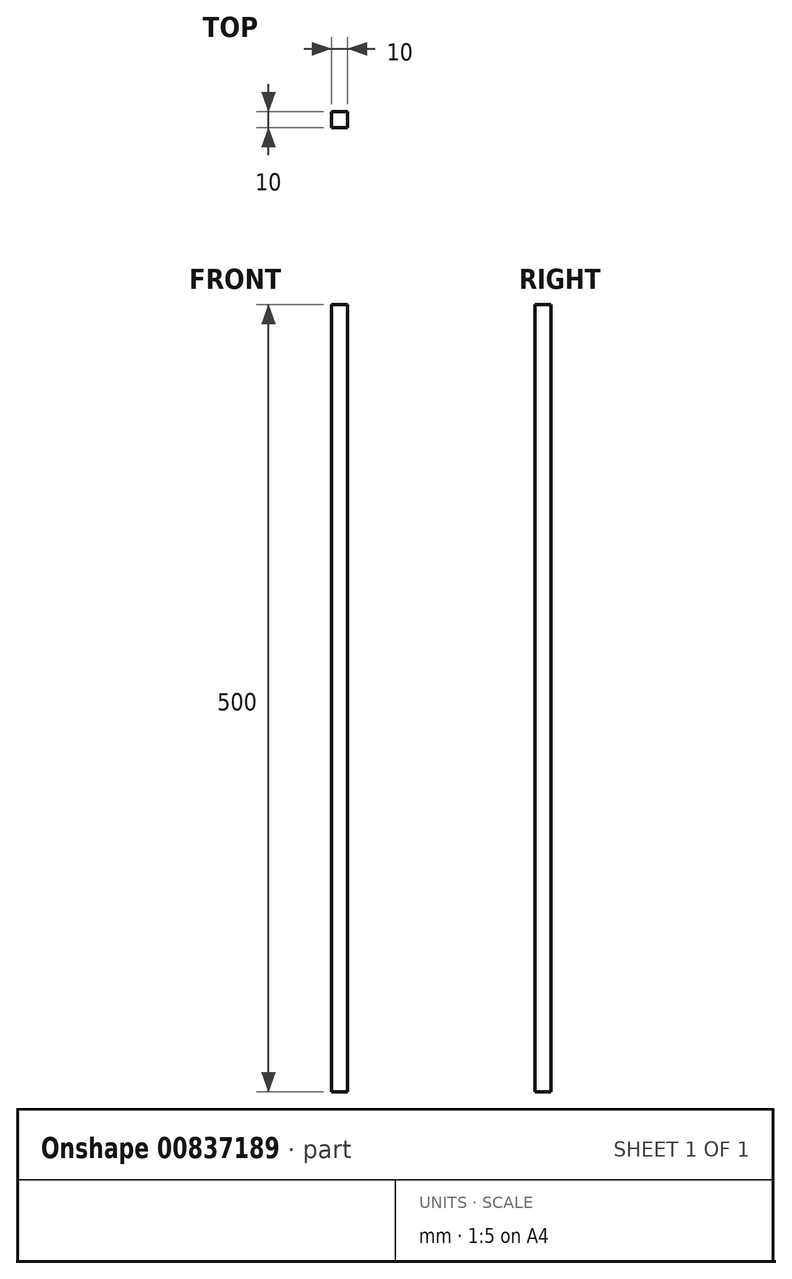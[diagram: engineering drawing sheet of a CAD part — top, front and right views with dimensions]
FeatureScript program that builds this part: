
annotation { "Feature Type Name" : "Feature", "Feature Type Description" : "" }
export const myFeature = defineFeature(function(context is Context, id is Id, definition is map)
    precondition{}
    {
        {
            assignVariable(context, id + "F0", {"name" : "length", "anyValue" : 500 * mm});
        }
        {
            var Q0;
            Q0=qCreatedBy(makeId("Top.planeOp"),FACE);
            var sketch = newSketch(context, id + "F1", { "sketchPlane" : qUnion([Q0])});
            skLineSegment(sketch, "E0.bottom", {"start": v(-50.91, -0.63) * mm, "end": v(-40.91, -0.63) * mm});
            skLineSegment(sketch, "E0.top", {"start": v(-50.91, -10.63) * mm, "end": v(-40.91, -10.63) * mm});
            skLineSegment(sketch, "E0.left", {"start": v(-50.91, -0.63) * mm, "end": v(-50.91, -10.63) * mm});
            skLineSegment(sketch, "E0.right", {"start": v(-40.91, -0.63) * mm, "end": v(-40.91, -10.63) * mm});
            skSolve(sketch);
        }
        {
            var Q0;
            Q0=makeQuery(id+"F1.imprint","IMPRINT",FACE,{"disambiguationData":[TD([[makeQuery(id+"F1.imprint","IMPRINT",EDGE,{"derivedFrom":sQuery(id+"F1.wireOp",EDGE,"E0.bottom")}),-1.0]])]});
            extrude(context, id + "F2", {"entities" : qUnion([Q0]), "depth" : getVariable(context, 'length'), "offsetDistance" : 25.4 * mm});
        }
    });
